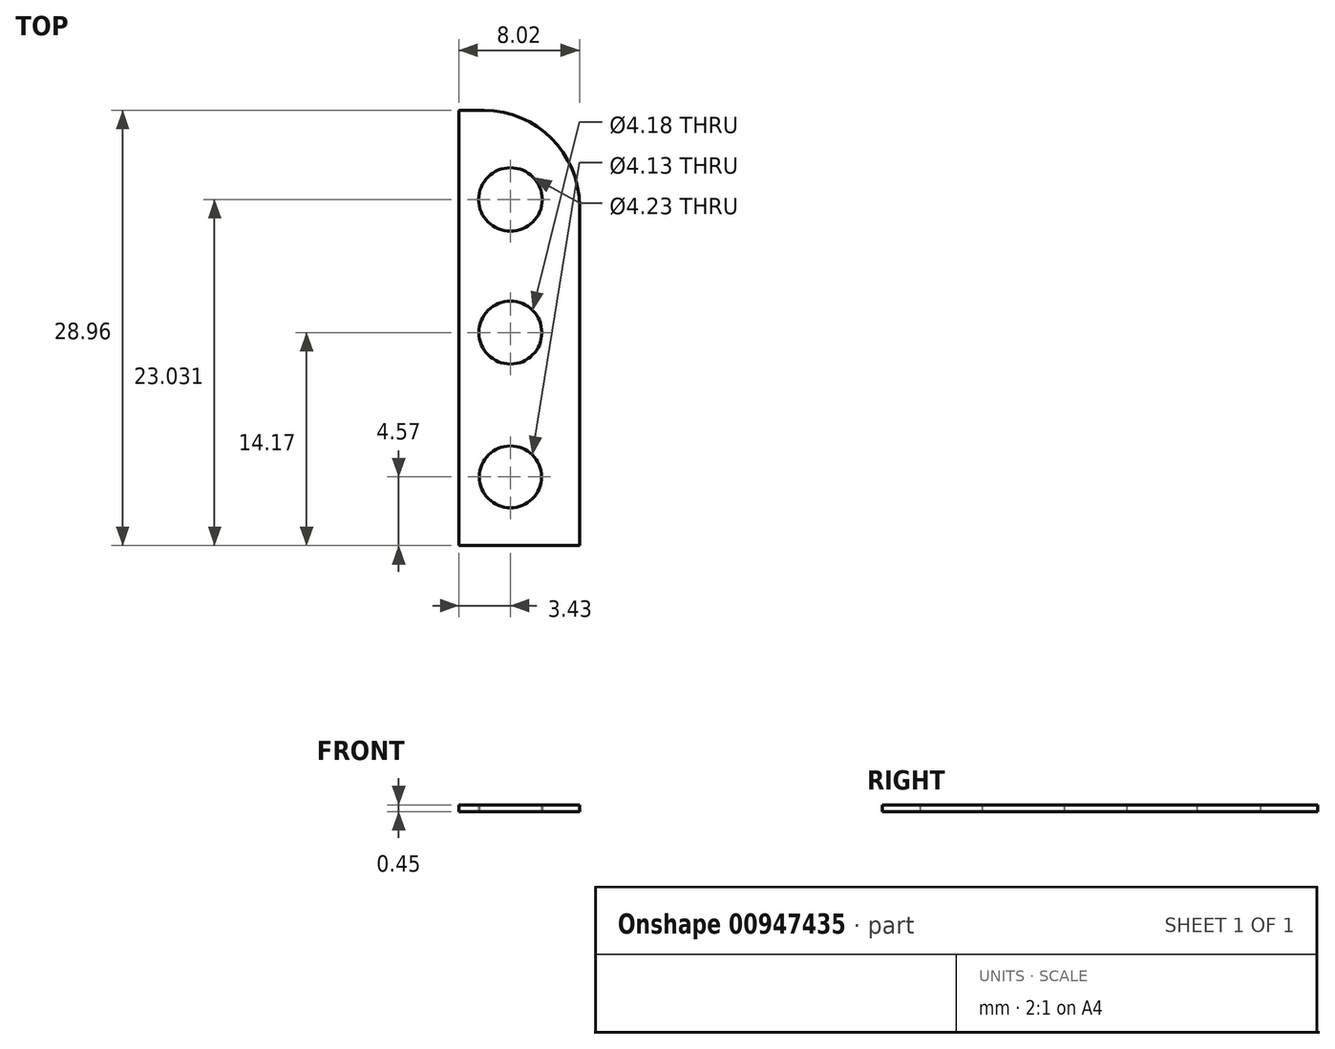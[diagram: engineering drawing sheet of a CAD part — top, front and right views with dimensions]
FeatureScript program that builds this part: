
annotation { "Feature Type Name" : "Feature", "Feature Type Description" : "" }
export const myFeature = defineFeature(function(context is Context, id is Id, definition is map)
    precondition{}
    {
        {
            var Q0;
            Q0=qCreatedBy(makeId("Top.planeOp"),FACE);
            var sketch = newSketch(context, id + "F0", { "sketchPlane" : qUnion([Q0])});
            skCircle(sketch, "E0", {"center": v(0, 0) * mm, "radius": 2.06 * mm});
            skLineSegment(sketch, "E1.bottom", {"start": v(4.6, -4.57) * mm, "end": v(-3.43, -4.57) * mm});
            skLineSegment(sketch, "E1.top", {"start": v(-1.76, 24.4) * mm, "end": v(-3.43, 24.4) * mm});
            skLineSegment(sketch, "E1.left", {"start": v(4.6, -4.57) * mm, "end": v(4.6, 18.04) * mm});
            skLineSegment(sketch, "E1.right", {"start": v(-3.43, -4.57) * mm, "end": v(-3.43, 24.4) * mm});
            skCircle(sketch, "E2", {"center": v(0, 9.6) * mm, "radius": 2.09 * mm});
            skCircle(sketch, "E3", {"center": v(0, 18.46) * mm, "radius": 2.12 * mm});
            skPoint(sketch, "E4.visualSharp", {"position": v(4.6, 24.4) * mm});
            skArc(sketch, "E4.filletArc", {"start": v(4.6, 18.04) * mm, "mid": v(2.73, 22.53) * mm, "end": v(-1.76, 24.4) * mm});
            skSolve(sketch);
        }
        {
            var Q0;
            Q0=makeQuery(id+"F0.imprint","IMPRINT",FACE,{"disambiguationData":[TD([[makeQuery(id+"F0.imprint","IMPRINT",EDGE,{"derivedFrom":sQuery(id+"F0.wireOp",EDGE,"E0")}),-1.0]])]});
            extrude(context, id + "F1", {"entities" : qUnion([Q0]), "depth" : .45 * mm, "offsetDistance" : 25.4 * mm});
        }
    });
